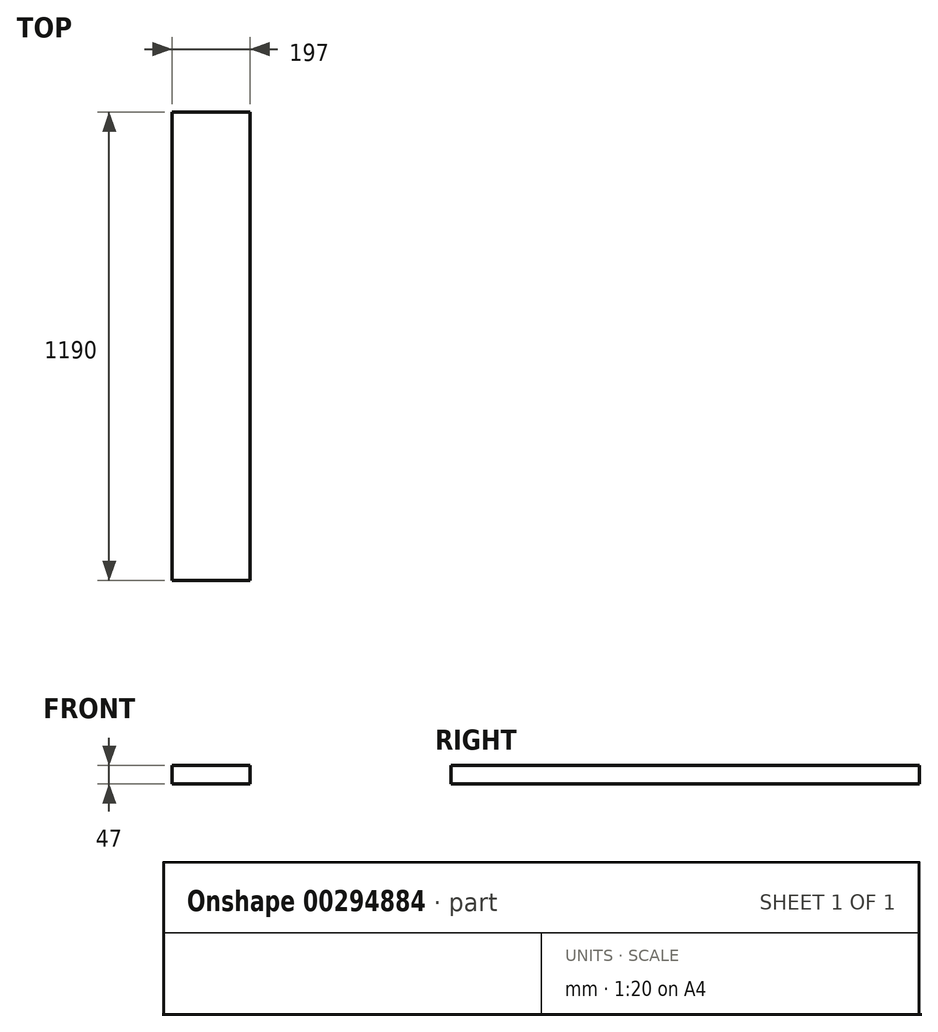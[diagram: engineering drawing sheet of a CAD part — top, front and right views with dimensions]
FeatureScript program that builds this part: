
annotation { "Feature Type Name" : "Feature", "Feature Type Description" : "" }
export const myFeature = defineFeature(function(context is Context, id is Id, definition is map)
    precondition{}
    {
        {
            var Q0;
            Q0=qCreatedBy(makeId("Front.planeOp"),FACE);
            var sketch = newSketch(context, id + "F0", { "sketchPlane" : qUnion([Q0])});
            skLineSegment(sketch, "E0.bottom", {"start": v(98.5, 23.5) * mm, "end": v(-98.5, 23.5) * mm});
            skLineSegment(sketch, "E0.top", {"start": v(98.5, -23.5) * mm, "end": v(-98.5, -23.5) * mm});
            skLineSegment(sketch, "E0.left", {"start": v(98.5, 23.5) * mm, "end": v(98.5, -23.5) * mm});
            skLineSegment(sketch, "E0.right", {"start": v(-98.5, 23.5) * mm, "end": v(-98.5, -23.5) * mm});
            skPoint(sketch, "E0.middle", {"position": v(0, 0) * mm});
            skSolve(sketch);
        }
        {
            var Q0;
            Q0 = qSketchRegion(id + "F0", true);
            extrude(context, id + "F1", {"entities" : qUnion([Q0]), "depth" : 1190 * mm});
        }
    });
